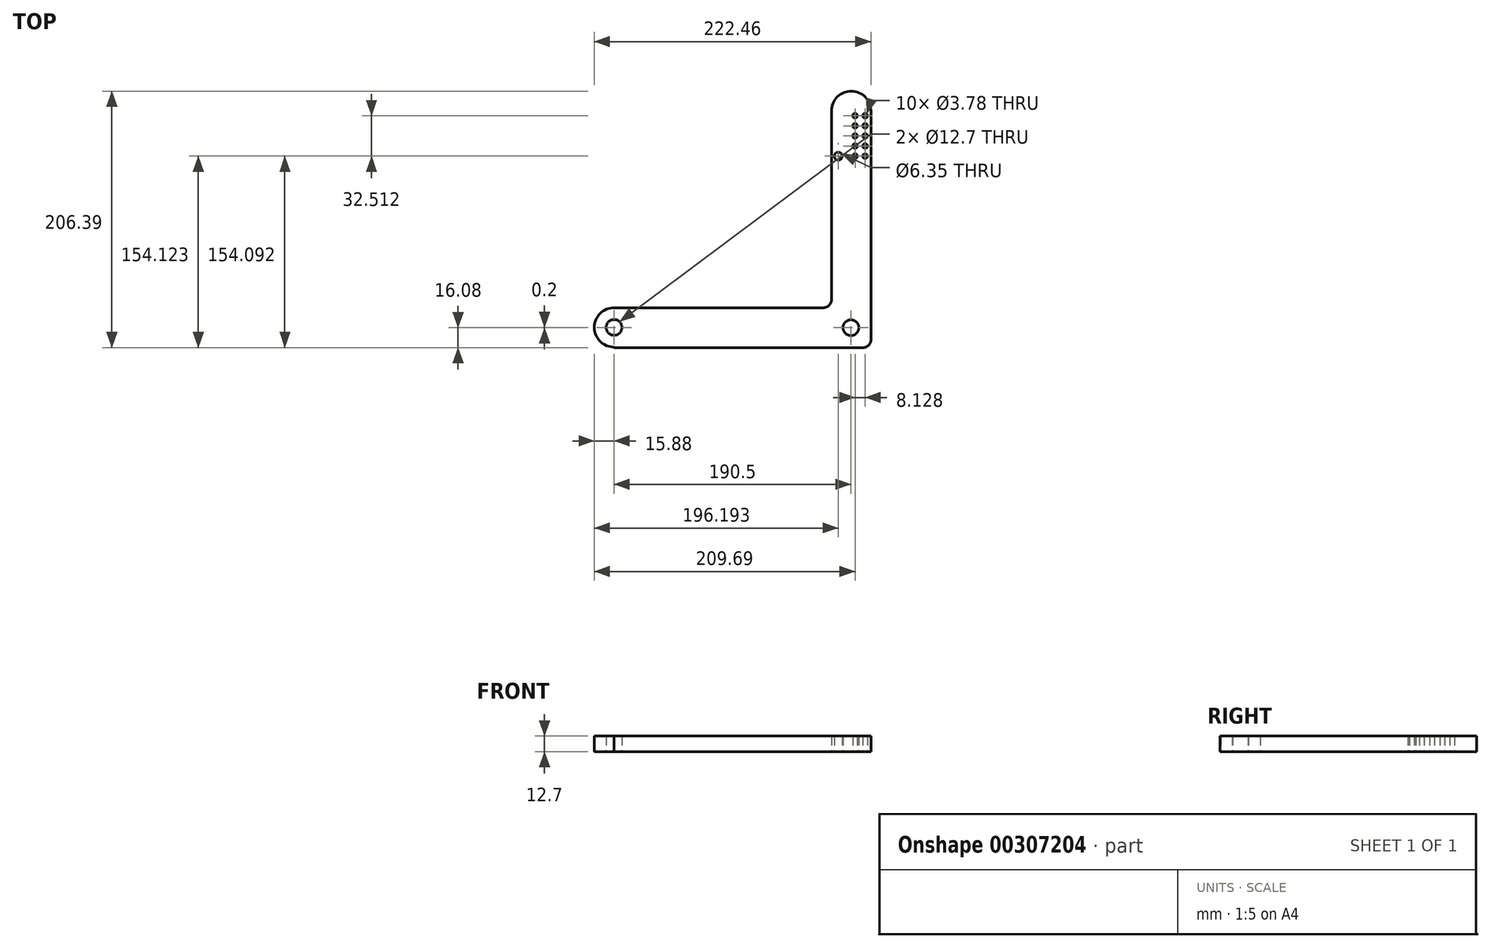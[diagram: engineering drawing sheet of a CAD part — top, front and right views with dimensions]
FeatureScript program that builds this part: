
annotation { "Feature Type Name" : "Feature", "Feature Type Description" : "" }
export const myFeature = defineFeature(function(context is Context, id is Id, definition is map)
    precondition{}
    {
        {
            var Q0;
            Q0=qCreatedBy(makeId("Top.planeOp"),FACE);
            var sketch = newSketch(context, id + "F0", { "sketchPlane" : qUnion([Q0])});
            skCircle(sketch, "E0", {"center": v(0, 0) * mm, "radius": 6.35 * mm});
            skArc(sketch, "E1", {"start": v(0, 15.88) * mm, "mid": v(-15.88, 0) * mm, "end": v(0, -15.88) * mm});
            skLineSegment(sketch, "E2.bottom", {"start": v(0, 15.88) * mm, "end": v(168.46, 15.88) * mm});
            skLineSegment(sketch, "E2.top", {"start": v(0, -16.28) * mm, "end": v(190.5, -16.28) * mm});
            skLineSegment(sketch, "E3.trimOffspring", {"start": v(0, -15.88) * mm, "end": v(0, -16.28) * mm});
            skPoint(sketch, "E4.firstSnap0", {"position": v(206.58, -0.2) * mm});
            skLineSegment(sketch, "E4.bottom", {"start": v(200.23, -16.28) * mm, "end": v(174.8, -16.28) * mm});
            skLineSegment(sketch, "E4.left", {"start": v(206.58, -9.93) * mm, "end": v(206.58, 174.22) * mm});
            skLineSegment(sketch, "E4.right", {"start": v(174.8, 22.23) * mm, "end": v(174.8, 174.22) * mm});
            skPoint(sketch, "E5.orphan", {"position": v(190.5, 15.88) * mm});
            skPoint(sketch, "E6.center.orphan", {"position": v(190.5, -0.2) * mm});
            skPoint(sketch, "E7.visualSharp", {"position": v(206.58, -16.28) * mm});
            skArc(sketch, "E7.filletArc", {"start": v(200.23, -16.28) * mm, "mid": v(204.72, -14.42) * mm, "end": v(206.58, -9.93) * mm});
            skPoint(sketch, "E8.visualSharp", {"position": v(174.8, 15.88) * mm});
            skArc(sketch, "E8.filletArc", {"start": v(168.46, 15.88) * mm, "mid": v(172.95, 17.74) * mm, "end": v(174.8, 22.23) * mm});
            skCircle(sketch, "E9", {"center": v(180.31, 137.81) * mm, "radius": 3.18 * mm});
            skCircle(sketch, "E10", {"center": v(193.8, 170.35) * mm, "radius": 1.9 * mm});
            skCircle(sketch, "E11.0.1.0", {"center": v(193.8, 162.23) * mm, "radius": 1.9 * mm});
            skCircle(sketch, "E11.0.2.0", {"center": v(193.8, 154.1) * mm, "radius": 1.9 * mm});
            skCircle(sketch, "E11.0.3.0", {"center": v(193.8, 145.97) * mm, "radius": 1.9 * mm});
            skCircle(sketch, "E11.0.4.0", {"center": v(193.8, 137.84) * mm, "radius": 1.9 * mm});
            skCircle(sketch, "E11.1.0.0", {"center": v(201.94, 170.35) * mm, "radius": 1.9 * mm});
            skCircle(sketch, "E11.1.1.0", {"center": v(201.94, 162.23) * mm, "radius": 1.9 * mm});
            skCircle(sketch, "E11.1.2.0", {"center": v(201.94, 154.1) * mm, "radius": 1.9 * mm});
            skCircle(sketch, "E11.1.3.0", {"center": v(201.94, 145.97) * mm, "radius": 1.9 * mm});
            skCircle(sketch, "E11.1.4.0", {"center": v(201.94, 137.84) * mm, "radius": 1.9 * mm});
            skLineSegment(sketch, "E11.direction1", {"start": v(193.8, 170.35) * mm, "end": v(201.94, 170.35) * mm, "construction": true});
            skLineSegment(sketch, "E11.direction2", {"start": v(193.8, 170.35) * mm, "end": v(193.8, 162.23) * mm, "construction": true});
            skArc(sketch, "E12", {"start": v(206.58, 174.22) * mm, "mid": v(190.7, 190.1) * mm, "end": v(174.8, 174.22) * mm});
            skCircle(sketch, "E13", {"center": v(190.5, -0.2) * mm, "radius": 6.35 * mm});
            skSolve(sketch);
        }
        {
            var Q0;
            Q0=makeQuery(id+"F0.imprint","IMPRINT",FACE,{"disambiguationData":[TD([[makeQuery(id+"F0.imprint","IMPRINT",EDGE,{"derivedFrom":sQuery(id+"F0.wireOp",EDGE,"E0")}),-1.0]])]});
            extrude(context, id + "F1", {"entities" : qUnion([Q0]), "depth" : 12.7 * mm});
        }
    });
